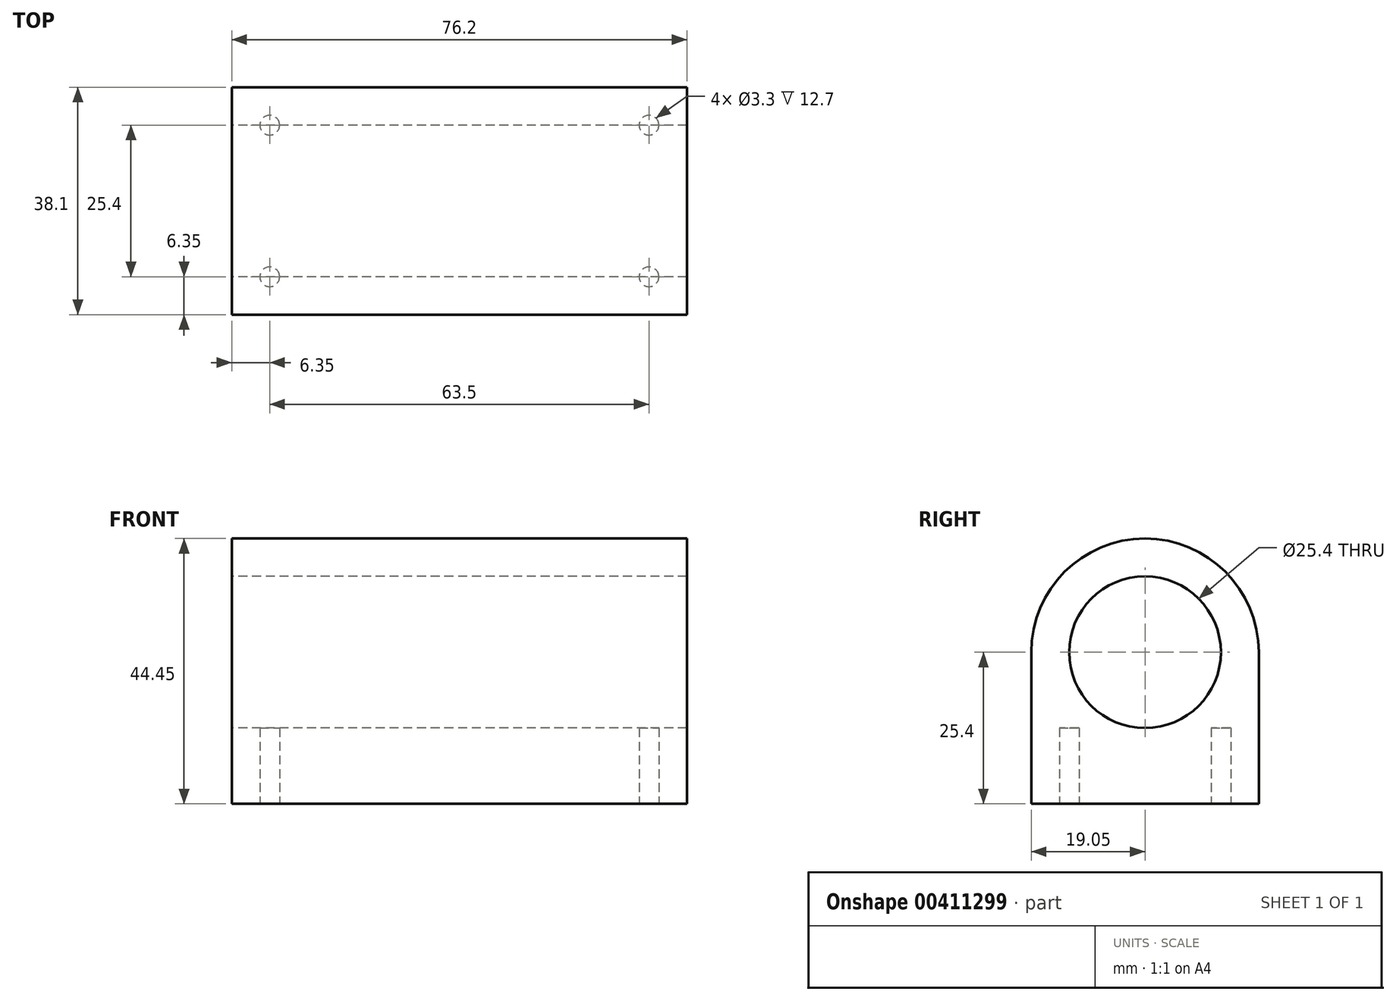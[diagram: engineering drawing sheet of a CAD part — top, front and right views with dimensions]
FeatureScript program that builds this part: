
annotation { "Feature Type Name" : "Feature", "Feature Type Description" : "" }
export const myFeature = defineFeature(function(context is Context, id is Id, definition is map)
    precondition{}
    {
        {
            var Q0;
            Q0=qCreatedBy(makeId("Right.planeOp"),FACE);
            var sketch = newSketch(context, id + "F0", { "sketchPlane" : qUnion([Q0])});
            skCircle(sketch, "E0", {"center": v(0, 0) * mm, "radius": 12.7 * mm});
            skCircle(sketch, "E1", {"center": v(0, 0) * mm, "radius": 19.05 * mm});
            skLineSegment(sketch, "E2", {"start": v(-19.05, 0) * mm, "end": v(-19.05, -25.4) * mm});
            skLineSegment(sketch, "E3", {"start": v(-19.05, -25.4) * mm, "end": v(19.05, -25.4) * mm});
            skLineSegment(sketch, "E4", {"start": v(19.05, -25.4) * mm, "end": v(19.05, 0) * mm});
            skSolve(sketch);
        }
        {
            var Q0;
            Q0 = qSketchRegion(id + "F0", true);
            extrude(context, id + "F1", {"entities" : qUnion([Q0]), "depth" : 76.2 * mm, "symmetric" : true});
        }
        {
            var Q0;
            Q0=makeQuery(id+"F1.opExtrude","SWEPT_FACE",FACE,{"disambiguationData":[OSD([sQuery(id+"F0.wireOp",EDGE,"E3")])]});
            var sketch = newSketch(context, id + "F2", { "sketchPlane" : qUnion([Q0])});
            skCircle(sketch, "E5", {"center": v(-31.75, 12.7) * mm, "radius": 1.65 * mm});
            skCircle(sketch, "E6", {"center": v(-31.75, -12.7) * mm, "radius": 1.65 * mm});
            skCircle(sketch, "E7", {"center": v(31.75, 12.7) * mm, "radius": 1.65 * mm});
            skCircle(sketch, "E8", {"center": v(31.75, -12.7) * mm, "radius": 1.65 * mm});
            skSolve(sketch);
        }
        {
            var Q0;
            Q0 = qSketchRegion(id + "F2", true);
            var Q1;
            Q1=makeQuery(id+"F1.opExtrude","SWEPT_FACE",FACE,{"disambiguationData":[OSD([sQuery(id+"F0.wireOp",EDGE,"E0")])]});
            extrude(context, id + "F3", {"entities" : qUnion([Q0]), "operationType" : NewBodyOperationType.REMOVE, "oppositeDirection" : true, "endBoundEntityFace" : qUnion([Q1]), "depth" : 12.7 * mm});
        }
    });
